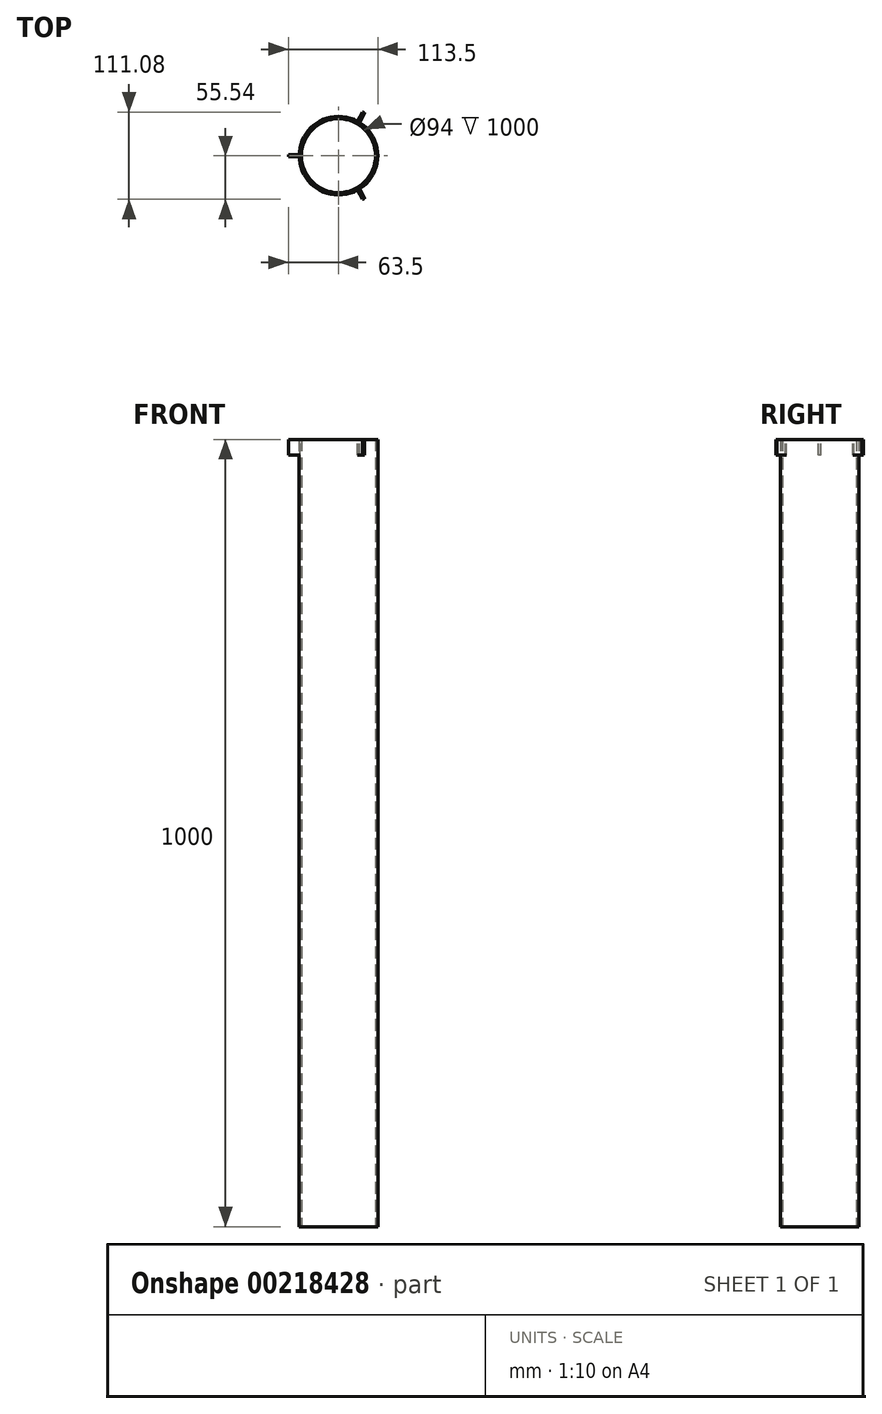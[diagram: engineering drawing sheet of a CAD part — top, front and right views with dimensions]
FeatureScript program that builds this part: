
annotation { "Feature Type Name" : "Feature", "Feature Type Description" : "" }
export const myFeature = defineFeature(function(context is Context, id is Id, definition is map)
    precondition{}
    {
        {
            var Q0;
            Q0=qCreatedBy(makeId("Front.planeOp"),FACE);
            var sketch = newSketch(context, id + "F0", { "sketchPlane" : qUnion([Q0])});
            skLineSegment(sketch, "E0", {"start": v(0.45, 2.22) * mm, "end": v(0.45, 1084.65) * mm});
            skSolve(sketch);
        }
        {
            var Q0;
            Q0=qCreatedBy(makeId("Top.planeOp"),FACE);
            var sketch = newSketch(context, id + "F1", { "sketchPlane" : qUnion([Q0])});
            skCircle(sketch, "E1", {"center": v(0, 0) * mm, "radius": 47 * mm});
            skCircle(sketch, "E2.0", {"center": v(0, 0) * mm, "radius": 50 * mm});
            skSolve(sketch);
        }
        {
            var Q0;
            Q0 = qSketchRegion(id + "F1", true);
            extrude(context, id + "F2", {"entities" : qUnion([Q0]), "flatOperationType" : FlatOperationType.REMOVE, "offsetDistance" : 25 * mm, "depth" : 1000 * mm, "domain" : OperationDomain.MODEL});
        }
        {
            var Q0;
            Q0=qCreatedBy(makeId("Top.planeOp"),FACE);
            cPlane(context, id + "F3", {"entities" : qUnion([Q0]), "cplaneType" : CPlaneType.OFFSET, "offset" : 1000 * mm, "width" : 150 * mm, "height" : 150 * mm});
        }
        {
            var Q0;
            Q0=qCreatedBy(id+"F3.planeOp",FACE);
            var sketch = newSketch(context, id + "F4", { "sketchPlane" : qUnion([Q0])});
            skLineSegment(sketch, "E3.bottom", {"start": v(-49, 1.5) * mm, "end": v(-64, 1.5) * mm});
            skLineSegment(sketch, "E3.top", {"start": v(-49, -1.5) * mm, "end": v(-64, -1.5) * mm});
            skLineSegment(sketch, "E3.left", {"start": v(-49, 1.5) * mm, "end": v(-49, -1.5) * mm});
            skLineSegment(sketch, "E3.right", {"start": v(-64, 1.5) * mm, "end": v(-64, -1.5) * mm});
            skPoint(sketch, "E3.middle", {"position": v(-56.5, 0) * mm});
            skSolve(sketch);
        }
        {
            var Q0;
            Q0 = qSketchRegion(id + "F4", true);
            extrude(context, id + "F5", {"entities" : qUnion([Q0]), "flatOperationType" : FlatOperationType.REMOVE, "oppositeDirection" : true, "offsetDistance" : 25 * mm, "depth" : 20 * mm, "domain" : OperationDomain.MODEL});
        }
        {
            var Q0;
            Q0=makeQuery(id+"F5.opExtrude","SWEPT_BODY",BODY,{"disambiguationData":[OSD([sQuery(id+"F4.wireOp",EDGE,"E3.bottom"),sQuery(id+"F4.wireOp",EDGE,"E3.top"),sQuery(id+"F4.wireOp",EDGE,"E3.left"),sQuery(id+"F4.wireOp",EDGE,"E3.right")])]});
            var Q1;
            Q1=sQuery(id+"F0.wireOp",EDGE,"E0");
            circularPattern(context, id + "F6", {"entities" : qUnion([Q0]), "axis" : qUnion([Q1]), "angle" : 360 * degree, "instanceCount" : 3, "equalSpace" : true});
        }
        {
            var Q0;
            Q0=qCreatedBy(id+"F3.planeOp",FACE);
            var sketch = newSketch(context, id + "F7", { "sketchPlane" : qUnion([Q0])});
            skCircle(sketch, "E4", {"center": v(0, 0) * mm, "radius": 63.5 * mm});
            skCircle(sketch, "E5.0", {"center": v(0, 0) * mm, "radius": 66.5 * mm});
            skSolve(sketch);
        }
        {
            var Q0;
            Q0=makeQuery(id+"F7.imprint","IMPRINT",FACE,{"disambiguationData":[TD([[makeQuery(id+"F7.imprint","IMPRINT",EDGE,{"derivedFrom":sQuery(id+"F7.wireOp",EDGE,"E4")}),-1.0]])]});
            extrude(context, id + "F8", {"entities" : qUnion([Q0]), "operationType" : NewBodyOperationType.REMOVE, "oppositeDirection" : true, "depth" : 20 * mm});
        }
    });
